# Revit family: Camera-Integrated-Panasonic-OutDoor_PTZ-4K_AW-UR100X
name_source: partatom
category: Communication Devices
units: mm (PartAtom-declared; Revit-internal decimal feet)

## family parameters
Cut with Voids When Loaded = No
Host = Face
Maintain Annotation Orientation = No
OmniClass Number = 23.85.10.14.11
OmniClass Title = Cameras
Part Type = Normal
Room Calculation Point = No
Round Connector Dimension = Use Diameter
Shared = No

## types (1)
- AW-UR100
    Date Last Modified = 2023/07/10
    Default Elevation = 0 mm  [stored 0 ft]
    Depth = 392 mm  [stored 1.28609 ft]
    Description = 4K Integrated OutDoor PTZ Camera AW-UR100
    Effective Pixels = Approx. 8,290,000
    Equipment Abbreviation = MPC
    Family Version = 1.0.0
    Gain = Auto、0dB~36dB (1 dB Step)
    Height = 367 mm  [stored 1.20407 ft]
    IR Panel Meterial = Panasonic - Target
    Image Sensor = 1/2.5-type(1/2.5 inch) 4K MOS×1
    LAN = LAN connector for IP control (RJ‑45)
    Lens Axis Offset = 10 mm  [stored 0.0328084 ft]
    Lens Material = Laminate, Navy
    Manufacturer = Panasonic Connect Co., Ltd.
    Manufacturer URL = https://connect.panasonic.com
    Minimum Illumination = 3.000 lx
    Model = AW-UR100
    Model Disclaimer = Contact Panasonic for more information
    Output Format = 2160/59.94p,2160/50p,2160/29.97p,2160/25p,2160/24p,2160/23.98p,1080/59.94p,1080/50p,1080/29.97p,1080/29.97PsF,1080/25p,1080/25PsF,1080/23.98p,1080/24p,1080/23.98p,1080/23.98PsF,1080/59.94i,1080/50i,720/59.94p,720/50p
    Pan Max = 175.000°
    Pan Min = -175.000°
    Panning Range = ±175°
    Part Description = 4K Integrated OutDoor PTZ Camera AW-UR100
    Part Number = AW-UR100
    Product Documentation Link = https://pro-av.panasonic.net
    Product Material = Paint - Panasonic - Silver
    Product Page URL = https://pro-av.panasonic.net
    Provide Feedback = https://www.surveymonkey.com
    Regulatory Compliance = UL,c-UL,FCC,IC(ｶﾅﾀﾞEMC),EMC,BIS,中国版/ｳｸﾗｲﾅRoHS,KCC
    Tilt Max = 30.000°
    Tilt Min = -210.000°
    Tilting Range = -30° to +210°
    URL = https://pro-av.panasonic.net
    Video In = G/L IN
    Video Out = 12G-SDI Out x 1, 3G-SDI Out x 1, SFP+ x 1
    Weight = 9.00 kgf
    Width = 258 mm  [stored 0.846457 ft]
    z Camera Head Origin Height = 173.6 mm
    z Const Pan Handle Length = 700 mm  [stored 2.29659 ft]
    z Const Tilt Base Length = 360 mm  [stored 1.1811 ft]
    z Const Tilt Base2 Length = 500 mm  [stored 1.64042 ft]
    z Const Tilt Handle Length = 360 mm  [stored 1.1811 ft]
    z Const Yaw Base Length = 250 mm  [stored 0.82021 ft]
    z Const Yaw Base2 Length = 500.000°
    z Const Yaw Handle Length = 235 mm  [stored 0.770997 ft]

note: [stored X ft] marks values corroborated as IEEE doubles in the binary element streams (Revit-internal decimal feet)

## geometry (parser evidence)
native form markers: Blend x2, Sweep x6
no freeform markers — native parametric forms only
